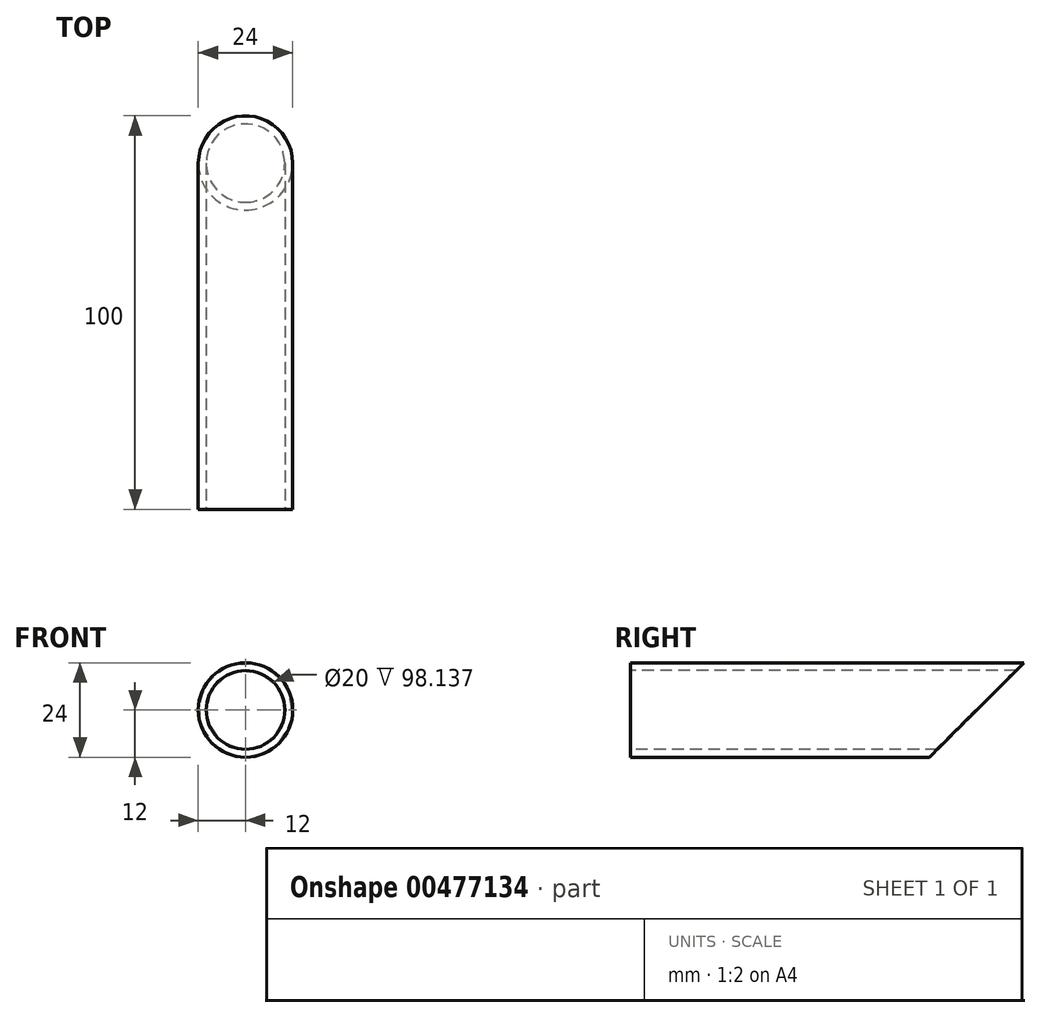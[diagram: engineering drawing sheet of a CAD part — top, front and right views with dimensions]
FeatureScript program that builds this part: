
annotation { "Feature Type Name" : "Feature", "Feature Type Description" : "" }
export const myFeature = defineFeature(function(context is Context, id is Id, definition is map)
    precondition{}
    {
        {
            var Q0;
            Q0=qCreatedBy(makeId("Front.planeOp"),FACE);
            var sketch = newSketch(context, id + "F0", { "sketchPlane" : qUnion([Q0])});
            skCircle(sketch, "E0", {"center": v(0, 0) * mm, "radius": 10 * mm});
            skCircle(sketch, "E1", {"center": v(0, 0) * mm, "radius": 12 * mm});
            skSolve(sketch);
        }
        {
            var Q0;
            Q0=makeQuery(id+"F0.imprint","IMPRINT",FACE,{"disambiguationData":[TD([[makeQuery(id+"F0.imprint","IMPRINT",EDGE,{"derivedFrom":sQuery(id+"F0.wireOp",EDGE,"E0")}),-1.0]])]});
            extrude(context, id + "F1", {"entities" : qUnion([Q0]), "oppositeDirection" : true, "depth" : 100 * mm, "offsetDistance" : 25 * mm});
        }
        {
            var Q0;
            Q0=qCreatedBy(makeId("Right.planeOp"),FACE);
            var sketch = newSketch(context, id + "F2", { "sketchPlane" : qUnion([Q0])});
            skLineSegment(sketch, "E2", {"start": v(100, 12) * mm, "end": v(76, -12) * mm});
            skLineSegment(sketch, "E3", {"start": v(76, -12) * mm, "end": v(100, -12) * mm});
            skLineSegment(sketch, "E4", {"start": v(100, -12) * mm, "end": v(100, 12) * mm});
            skLineSegment(sketch, "E5.0", {"start": v(100, -12) * mm, "end": v(100, 12) * mm, "construction": true});
            skLineSegment(sketch, "E6", {"start": v(100, -12) * mm, "end": v(0, -12) * mm, "construction": true});
            skSolve(sketch);
        }
        {
            var Q0;
            Q0 = qSketchRegion(id + "F2", true);
            extrude(context, id + "F3", {"entities" : qUnion([Q0]), "operationType" : NewBodyOperationType.REMOVE, "endBound" : BoundingType.THROUGH_ALL, "oppositeDirection" : true, "depth" : 25 * mm, "offsetDistance" : 25 * mm, "hasSecondDirection" : true, "secondDirectionBound" : SecondDirectionBoundingType.THROUGH_ALL, "secondDirectionOppositeDirection" : false, "secondDirectionDepth" : 25 * mm});
        }
    });
